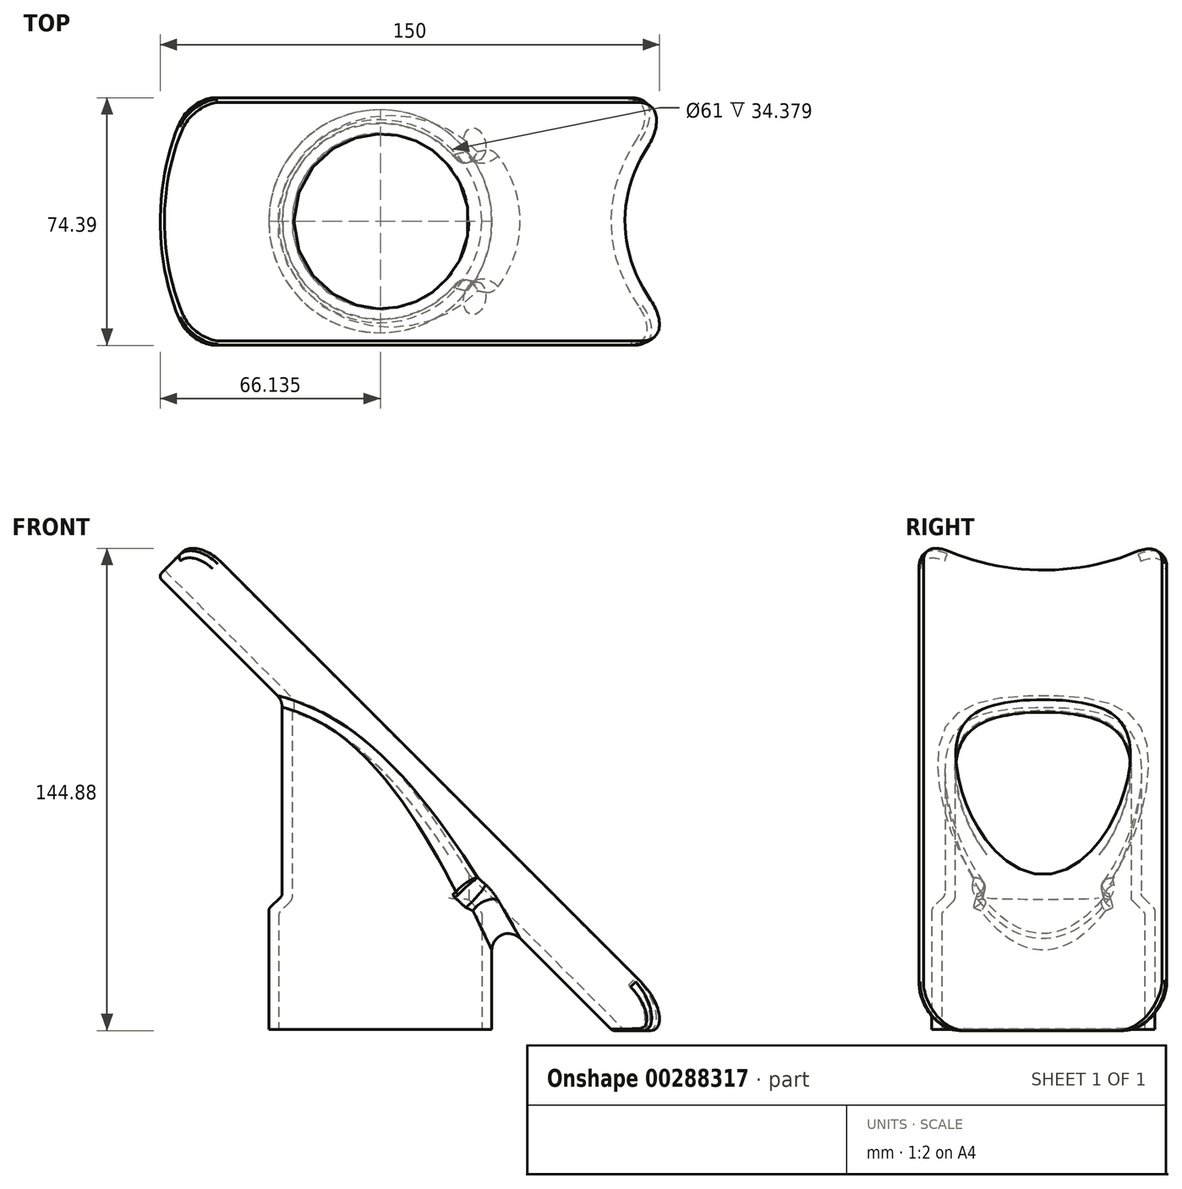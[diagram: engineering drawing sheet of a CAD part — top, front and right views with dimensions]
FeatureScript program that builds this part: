
annotation { "Feature Type Name" : "Feature", "Feature Type Description" : "" }
export const myFeature = defineFeature(function(context is Context, id is Id, definition is map)
    precondition{}
    {
        {
            var Q0;
            Q0=qCreatedBy(makeId("Front.planeOp"),FACE);
            var sketch = newSketch(context, id + "F0", { "sketchPlane" : qUnion([Q0])});
            skLineSegment(sketch, "E0", {"start": v(30.18, 0.33) * mm, "end": v(30.18, 34.7) * mm});
            skLineSegment(sketch, "E1", {"start": v(26.18, 39.95) * mm, "end": v(26.18, 135.33) * mm});
            skLineSegment(sketch, "E2", {"start": v(26.18, 135.33) * mm, "end": v(29.18, 135.33) * mm});
            skLineSegment(sketch, "E3", {"start": v(29.18, 135.33) * mm, "end": v(29.18, 41.2) * mm});
            skLineSegment(sketch, "E4", {"start": v(33.18, 35.95) * mm, "end": v(33.18, 0.33) * mm});
            skLineSegment(sketch, "E5", {"start": v(33.18, 0.33) * mm, "end": v(30.18, 0.33) * mm});
            skLineSegment(sketch, "E6", {"start": v(-0.32, 0.33) * mm, "end": v(-0.32, 150.33) * mm, "construction": true});
            skPoint(sketch, "E7.visualSharp", {"position": v(30.18, 35.33) * mm});
            skLineSegment(sketch, "E8", {"start": v(29.74, 35.77) * mm, "end": v(26.61, 38.89) * mm});
            skArc(sketch, "E9.filletArc", {"start": v(30.18, 34.7) * mm, "mid": v(30.06, 35.28) * mm, "end": v(29.74, 35.77) * mm});
            skPoint(sketch, "E10.visualSharp", {"position": v(26.18, 39.33) * mm});
            skArc(sketch, "E10.filletArc", {"start": v(26.18, 39.95) * mm, "mid": v(26.29, 39.38) * mm, "end": v(26.61, 38.89) * mm});
            skLineSegment(sketch, "E11.0", {"start": v(32.74, 37.01) * mm, "end": v(29.61, 40.13) * mm});
            skPoint(sketch, "E12.visualSharp", {"position": v(33.18, 36.57) * mm});
            skArc(sketch, "E12.filletArc", {"start": v(33.18, 35.95) * mm, "mid": v(33.06, 36.52) * mm, "end": v(32.74, 37.01) * mm});
            skPoint(sketch, "E13.visualSharp", {"position": v(29.18, 40.57) * mm});
            skArc(sketch, "E13.filletArc", {"start": v(29.18, 41.2) * mm, "mid": v(29.29, 40.62) * mm, "end": v(29.61, 40.13) * mm});
            skPoint(sketch, "E14.orphan", {"position": v(-0.32, 150.33) * mm});
            skLineSegment(sketch, "E15", {"start": v(-0.32, 150.33) * mm, "end": v(150, 0) * mm, "construction": true});
            skSolve(sketch);
        }
        {
            var Q0;
            Q0=makeQuery(id+"F0.imprint","IMPRINT",FACE,{"disambiguationData":[TD([[makeQuery(id+"F0.imprint","IMPRINT",EDGE,{"derivedFrom":sQuery(id+"F0.wireOp",EDGE,"E0")}),-1.0]])]});
            var Q1;
            Q1=sQuery(id+"F0.wireOp",EDGE,"E6");
            revolve(context, id + "F1", {"entities" : qUnion([Q0]), "axis" : qUnion([Q1]), "revolveType" : RevolveType.FULL});
        }
        {
            var Q0;
            Q0=sQuery(id+"F0.wireOp",EDGE,"E15");
            var Q1;
            Q1=sQuery(id+"F0.wireOp",VERTEX,"E15.end");
            cPlane(context, id + "F2", {"entities" : qUnion([Q0, Q1]), "cplaneType" : CPlaneType.LINE_POINT, "offset" : 25 * mm, "width" : 150 * mm, "height" : 150 * mm});
        }
        {
            var Q0;
            Q0=qCreatedBy(id+"F2.planeOp",FACE);
            var sketch = newSketch(context, id + "F3", { "sketchPlane" : qUnion([Q0])});
            skArc(sketch, "E16", {"start": v(-35.93, 65.49) * mm, "mid": v(-0.17, 52.07) * mm, "end": v(35.67, 65.26) * mm});
            skArc(sketch, "E17.0", {"start": v(-37.9, 63.22) * mm, "mid": v(0, 49.07) * mm, "end": v(37.9, 63.22) * mm});
            skLineSegment(sketch, "E18", {"start": v(-37.9, 63.22) * mm, "end": v(-35.93, 65.49) * mm});
            skLineSegment(sketch, "E19", {"start": v(-37.9, 63.22) * mm, "end": v(44.37, 63.22) * mm, "construction": true});
            skLineSegment(sketch, "E20", {"start": v(37.9, 63.22) * mm, "end": v(35.67, 65.26) * mm});
            skSolve(sketch);
        }
        {
            var Q0;
            Q0=makeQuery(id+"F3.imprint","IMPRINT",FACE,{"disambiguationData":[TD([[makeQuery(id+"F3.imprint","IMPRINT",EDGE,{"derivedFrom":sQuery(id+"F3.wireOp",EDGE,"E16")}),-1.0]])]});
            extrude(context, id + "F4", {"entities" : qUnion([Q0]), "oppositeDirection" : true, "depth" : 250 * mm});
        }
        {
            var Q0;
            Q0=qCreatedBy(id+"F2.planeOp",FACE);
            var sketch = newSketch(context, id + "F5", { "sketchPlane" : qUnion([Q0])});
            skCircle(sketch, "E21", {"center": v(0, 105.74) * mm, "radius": 54 * mm});
            skSolve(sketch);
        }
        {
            var Q0;
            Q0=makeQuery(id+"F5.imprint","IMPRINT",FACE,{"disambiguationData":[TD([[makeQuery(id+"F5.imprint","IMPRINT",EDGE,{"derivedFrom":sQuery(id+"F5.wireOp",EDGE,"E21")}),1.0]])]});
            extrude(context, id + "F6", {"entities" : qUnion([Q0]), "operationType" : NewBodyOperationType.REMOVE, "oppositeDirection" : true, "depth" : 250 * mm});
        }
        {
            var Q0;
            Q0=qCreatedBy(makeId("Top.planeOp"),FACE);
            var sketch = newSketch(context, id + "F7", { "sketchPlane" : qUnion([Q0])});
            skCircle(sketch, "E22", {"center": v(0, 0) * mm, "radius": 26.25 * mm});
            skSolve(sketch);
        }
        {
            var Q0;
            Q0=makeQuery(id+"F7.imprint","IMPRINT",FACE,{"disambiguationData":[TD([[makeQuery(id+"F7.imprint","IMPRINT",EDGE,{"derivedFrom":sQuery(id+"F7.wireOp",EDGE,"E22")}),1.0]])]});
            var Q1;
            Q1=sQuery(id+"F7.wireOp",EDGE,"E22");
            extrude(context, id + "F8", {"entities" : qUnion([Q0]), "operationType" : NewBodyOperationType.REMOVE, "surfaceEntities" : qUnion([Q1]), "depth" : 150 * mm});
        }
        {
            var Q0;
            Q0=qCreatedBy(makeId("Front.planeOp"),FACE);
            var sketch = newSketch(context, id + "F9", { "sketchPlane" : qUnion([Q0])});
            skLineSegment(sketch, "E23.bottom", {"start": v(0, 0) * mm, "end": v(150.27, 0) * mm});
            skLineSegment(sketch, "E23.top", {"start": v(0, -49.88) * mm, "end": v(150.27, -49.88) * mm});
            skLineSegment(sketch, "E23.left", {"start": v(0, 0) * mm, "end": v(0, -49.88) * mm});
            skLineSegment(sketch, "E23.right", {"start": v(150.27, 0) * mm, "end": v(150.27, -49.88) * mm});
            skSolve(sketch);
        }
        {
            var Q0;
            Q0=makeQuery(id+"F9.imprint","IMPRINT",FACE,{"disambiguationData":[TD([[makeQuery(id+"F9.imprint","IMPRINT",EDGE,{"derivedFrom":sQuery(id+"F9.wireOp",EDGE,"E23.bottom")}),-1.0]])]});
            extrude(context, id + "F10", {"entities" : qUnion([Q0]), "operationType" : NewBodyOperationType.REMOVE, "endBound" : BoundingType.SYMMETRIC, "oppositeDirection" : true, "depth" : 100 * mm});
        }
        {
            var Q0;
            Q0=makeQuery(id+"F4.opExtrude","CAP_EDGE",EDGE,{"disambiguationData":[OSD([sQuery(id+"F3.wireOp",EDGE,"E20")])],"isStart":false});
            fillet(context, id + "F11", {"entities" : qUnion([Q0]), "radius" : 10 * mm, "tangentPropagation" : true, "allowEdgeOverflow" : false});
        }
        {
            var Q0;
            Q0=makeQuery(id+"F4.opExtrude","CAP_EDGE",EDGE,{"disambiguationData":[OSD([sQuery(id+"F3.wireOp",EDGE,"E18")])],"isStart":false});
            fillet(context, id + "F12", {"entities" : qUnion([Q0]), "radius" : 10 * mm, "tangentPropagation" : true, "allowEdgeOverflow" : false});
        }
        {
            var Q0;
            Q0=makeQuery(id+"F10.boolean.opBoolean","INTERSECT",EDGE,{"derivedFrom":[makeQuery(id+"F4.opExtrude","SWEPT_FACE",FACE,{"disambiguationData":[OSD([sQuery(id+"F3.wireOp",EDGE,"E18")])]}),makeQuery(id+"F10.opExtrude","SWEPT_FACE",FACE,{"disambiguationData":[OSD([sQuery(id+"F9.wireOp",EDGE,"E23.bottom")])]})]});
            fillet(context, id + "F13", {"entities" : qUnion([Q0]), "radius" : 10 * mm, "tangentPropagation" : true, "allowEdgeOverflow" : false});
        }
        {
            var Q0;
            Q0=makeQuery(id+"F10.boolean.opBoolean","INTERSECT",EDGE,{"derivedFrom":[makeQuery(id+"F4.opExtrude","SWEPT_FACE",FACE,{"disambiguationData":[OSD([sQuery(id+"F3.wireOp",EDGE,"E20")])]}),makeQuery(id+"F10.opExtrude","SWEPT_FACE",FACE,{"disambiguationData":[OSD([sQuery(id+"F9.wireOp",EDGE,"E23.bottom")])]})]});
            fillet(context, id + "F14", {"entities" : qUnion([Q0]), "radius" : 10 * mm, "tangentPropagation" : true, "allowEdgeOverflow" : false});
        }
        {
            var Q0;
            Q0=makeQuery(id+"F4.opExtrude","SWEPT_EDGE",EDGE,{"disambiguationData":[OSD([sQuery(id+"F3.wireOp",EDGE,"E17.0"),sQuery(id+"F3.wireOp",EDGE,"E18")])]});
            fillet(context, id + "F15", {"entities" : qUnion([Q0]), "radius" : 1.5 * mm, "tangentPropagation" : true, "allowEdgeOverflow" : false});
        }
        {
            var Q0;
            Q0=makeQuery(id+"F4.opExtrude","SWEPT_BODY",BODY,{"disambiguationData":[OSD([sQuery(id+"F3.wireOp",EDGE,"E16"),sQuery(id+"F3.wireOp",EDGE,"E17.0"),sQuery(id+"F3.wireOp",EDGE,"E18"),sQuery(id+"F3.wireOp",EDGE,"E20")])]});
            var Q1;
            Q1=makeQuery(id+"F1.opRevolve","SWEPT_BODY",BODY,{"disambiguationData":[OSD([sQuery(id+"F0.wireOp",EDGE,"E0"),sQuery(id+"F0.wireOp",EDGE,"E1"),sQuery(id+"F0.wireOp",EDGE,"E2"),sQuery(id+"F0.wireOp",EDGE,"E3"),sQuery(id+"F0.wireOp",EDGE,"E4"),sQuery(id+"F0.wireOp",EDGE,"E5"),sQuery(id+"F0.wireOp",EDGE,"E8"),sQuery(id+"F0.wireOp",EDGE,"E9.filletArc"),sQuery(id+"F0.wireOp",EDGE,"E10.filletArc"),sQuery(id+"F0.wireOp",EDGE,"E11.0"),sQuery(id+"F0.wireOp",EDGE,"E12.filletArc"),sQuery(id+"F0.wireOp",EDGE,"E13.filletArc")])]});
            booleanBodies(context, id + "F16", {"operationType" : BooleanOperationType.UNION, "tools" : qUnion([Q0, Q1])});
        }
        {
            var Q0;
            Q0=makeQuery(id+"F16.opBoolean","INTERSECT",EDGE,{"derivedFrom":[makeQuery(id+"F1.opRevolve","SWEPT_FACE",FACE,{"disambiguationData":[OSD([sQuery(id+"F0.wireOp",EDGE,"E3")])]}),makeQuery(id+"F4.opExtrude","SWEPT_FACE",FACE,{"disambiguationData":[OSD([sQuery(id+"F3.wireOp",EDGE,"E17.0")])]})]});
            fillet(context, id + "F17", {"entities" : qUnion([Q0]), "radius" : 5 * mm, "tangentPropagation" : true, "allowEdgeOverflow" : false});
        }
    });
